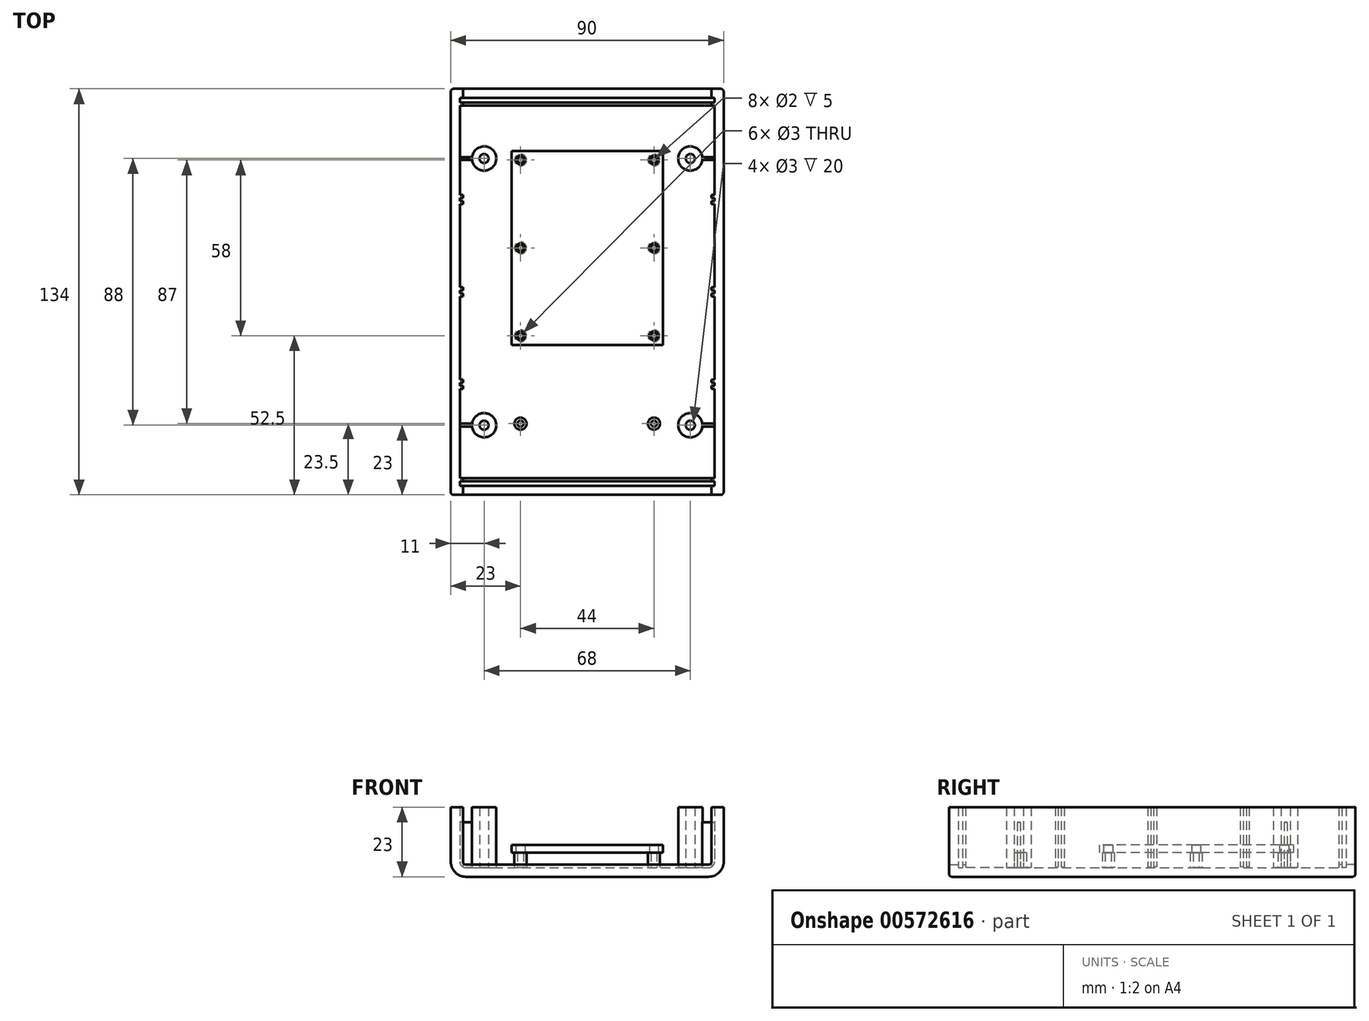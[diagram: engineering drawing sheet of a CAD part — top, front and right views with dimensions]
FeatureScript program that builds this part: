
annotation { "Feature Type Name" : "Feature", "Feature Type Description" : "" }
export const myFeature = defineFeature(function(context is Context, id is Id, definition is map)
    precondition{}
    {
        {
            var Q0;
            Q0=qCreatedBy(makeId("Top.planeOp"),FACE);
            var sketch = newSketch(context, id + "F0", { "sketchPlane" : qUnion([Q0])});
            skLineSegment(sketch, "E0.bottom", {"start": v(-44, 67) * mm, "end": v(-41, 67) * mm});
            skLineSegment(sketch, "E0.top", {"start": v(-45, 0) * mm, "end": v(-42, 0) * mm});
            skLineSegment(sketch, "E0.left", {"start": v(-45, 66) * mm, "end": v(-45, 0) * mm});
            skLineSegment(sketch, "E0.right", {"start": v(-41, 67) * mm, "end": v(-41, 64) * mm});
            skPoint(sketch, "E1.visualSharp", {"position": v(-45, 67) * mm});
            skArc(sketch, "E1.filletArc", {"start": v(-44, 67) * mm, "mid": v(-44.7, 66.7) * mm, "end": v(-45, 66) * mm});
            skLineSegment(sketch, "E2.bottom", {"start": v(-41, 64) * mm, "end": v(-42, 64) * mm});
            skLineSegment(sketch, "E2.top", {"start": v(-41, 62.5) * mm, "end": v(-42, 62.5) * mm});
            skLineSegment(sketch, "E2.right", {"start": v(-42, 64) * mm, "end": v(-42, 62.5) * mm});
            skLineSegment(sketch, "E3.trimOffspring", {"start": v(-41, 62.5) * mm, "end": v(-41, 61.5) * mm});
            skLineSegment(sketch, "E4.bottom", {"start": v(-41, 32) * mm, "end": v(-42, 32) * mm});
            skLineSegment(sketch, "E4.top", {"start": v(-41, 61.5) * mm, "end": v(-42, 61.5) * mm});
            skLineSegment(sketch, "E4.right", {"start": v(-42, 32) * mm, "end": v(-42, 61.5) * mm});
            skLineSegment(sketch, "E5.top", {"start": v(-41, 0.5) * mm, "end": v(-42, 0.5) * mm});
            skLineSegment(sketch, "E5.right", {"start": v(-42, 0) * mm, "end": v(-42, 0.5) * mm});
            skLineSegment(sketch, "E6.trimOffspring", {"start": v(-41, 32) * mm, "end": v(-41, 31) * mm});
            skPoint(sketch, "E7.orphan", {"position": v(-41, 0) * mm});
            skLineSegment(sketch, "E8.bottom", {"start": v(-41, 31) * mm, "end": v(-42, 31) * mm});
            skLineSegment(sketch, "E8.top", {"start": v(-41, 30) * mm, "end": v(-42, 30) * mm});
            skLineSegment(sketch, "E8.right", {"start": v(-42, 31) * mm, "end": v(-42, 30) * mm});
            skLineSegment(sketch, "E9.trimOffspring", {"start": v(-41, 30) * mm, "end": v(-41, 29) * mm});
            skLineSegment(sketch, "E10.bottom", {"start": v(-41, 29) * mm, "end": v(-42, 29) * mm});
            skLineSegment(sketch, "E10.top", {"start": v(-41, 1.5) * mm, "end": v(-42, 1.5) * mm});
            skLineSegment(sketch, "E10.right", {"start": v(-42, 29) * mm, "end": v(-42, 1.5) * mm});
            skLineSegment(sketch, "E11.trimOffspring", {"start": v(-41, 1.5) * mm, "end": v(-41, 0.5) * mm});
            skSolve(sketch);
        }
        {
            var Q0;
            Q0=qCreatedBy(makeId("Front.planeOp"),FACE);
            var sketch = newSketch(context, id + "F1", { "sketchPlane" : qUnion([Q0])});
            skPoint(sketch, "E12.0", {"position": v(-45, 0) * mm});
            skLineSegment(sketch, "E13", {"start": v(-45, 0) * mm, "end": v(-45, -18) * mm});
            skLineSegment(sketch, "E14", {"start": v(-40, -23) * mm, "end": v(0, -23) * mm});
            skPoint(sketch, "E15.visualSharp", {"position": v(-45, -23) * mm});
            skArc(sketch, "E15.filletArc", {"start": v(-45, -18) * mm, "mid": v(-43.54, -21.54) * mm, "end": v(-40, -23) * mm});
            skSolve(sketch);
        }
        {
            var Q0;
            Q0 = qSketchRegion(id + "F0", true);
            var Q1;
            Q1 = qConstructionFilter(qBodyType(qCreatedBy(id + "F1" ,EDGE), BodyType.WIRE), ConstructionObject.NO);
            sweep(context, id + "F2", {"profiles" : qUnion([Q0]), "path" : qUnion([Q1])});
        }
        {
            var Q0;
            Q0=qCreatedBy(makeId("Front.planeOp"),FACE);
            var sketch = newSketch(context, id + "F3", { "sketchPlane" : qUnion([Q0])});
            skLineSegment(sketch, "E16.bottom", {"start": v(0, -13.34) * mm, "end": v(-41, -13.34) * mm});
            skLineSegment(sketch, "E16.top", {"start": v(0, -20) * mm, "end": v(-40, -20) * mm});
            skLineSegment(sketch, "E16.left", {"start": v(0, -13.34) * mm, "end": v(0, -20) * mm});
            skLineSegment(sketch, "E16.right", {"start": v(-41, -13.34) * mm, "end": v(-41, -19.73) * mm});
            skLineSegment(sketch, "E17.0", {"start": v(-40, -20) * mm, "end": v(0, -20) * mm});
            skArc(sketch, "E18.0", {"start": v(-41, -19.73) * mm, "mid": v(-40.52, -19.93) * mm, "end": v(-40, -20) * mm});
            skPoint(sketch, "E19.orphan", {"position": v(-42, -18) * mm});
            skLineSegment(sketch, "E20.0", {"start": v(-41, 0) * mm, "end": v(-41, -13.34) * mm, "construction": true});
            skPoint(sketch, "E21.orphan", {"position": v(-41, -18) * mm});
            skSolve(sketch);
        }
        {
            var Q0;
            Q0 = qSketchRegion(id + "F3", true);
            extrude(context, id + "F4", {"entities" : qUnion([Q0]), "operationType" : NewBodyOperationType.REMOVE, "oppositeDirection" : true, "depth" : 40 * mm, "offsetDistance" : 25 * mm});
        }
        {
            var Q0;
            {var subQ0=sQuery(id+"F1.wireOp",EDGE,"E14");Q0=makeQuery(id+"F4.boolean.opBoolean","MERGE",FACE,{"derivedFrom":[makeQuery(id+"F2.opSweep","SWEPT_FACE",FACE,{"disambiguationData":[OSD([sQuery(id+"F0.wireOp",EDGE,"E4.right"),subQ0])]}),makeQuery(id+"F2.opSweep","SWEPT_FACE",FACE,{"disambiguationData":[OSD([sQuery(id+"F0.wireOp",EDGE,"E5.right"),subQ0])]}),makeQuery(id+"F2.opSweep","SWEPT_FACE",FACE,{"disambiguationData":[OSD([sQuery(id+"F0.wireOp",EDGE,"E8.right"),subQ0])]}),makeQuery(id+"F2.opSweep","SWEPT_FACE",FACE,{"disambiguationData":[OSD([sQuery(id+"F0.wireOp",EDGE,"E10.right"),subQ0])]}),makeQuery(id+"F4.opExtrude","SWEPT_FACE",FACE,{"disambiguationData":[OSD([sQuery(id+"F3.wireOp",EDGE,"E17.0")])]})]});}
            var sketch = newSketch(context, id + "F5", { "sketchPlane" : qUnion([Q0])});
            skCircle(sketch, "E22", {"center": v(-34, 44) * mm, "radius": 4 * mm});
            skCircle(sketch, "E23", {"center": v(-34, 44) * mm, "radius": 1.5 * mm});
            skCircle(sketch, "E24", {"center": v(-22, 43.5) * mm, "radius": 2 * mm});
            skCircle(sketch, "E25", {"center": v(-22, 43.5) * mm, "radius": 1 * mm});
            skCircle(sketch, "E26.0.1.0", {"center": v(-22, 14.5) * mm, "radius": 2 * mm});
            skCircle(sketch, "E26.0.1.1", {"center": v(-22, 14.5) * mm, "radius": 1 * mm});
            skLineSegment(sketch, "E26.direction1", {"start": v(-22, 43.5) * mm, "end": v(-7.59, 43.5) * mm, "construction": true});
            skLineSegment(sketch, "E26.direction2", {"start": v(-22, 43.5) * mm, "end": v(-22, 14.5) * mm, "construction": true});
            skLineSegment(sketch, "E27.bottom", {"start": v(-37.97, 43.5) * mm, "end": v(-42, 43.5) * mm});
            skLineSegment(sketch, "E27.top", {"start": v(-37.97, 44.5) * mm, "end": v(-42, 44.5) * mm});
            skLineSegment(sketch, "E27.right", {"start": v(-42, 43.5) * mm, "end": v(-42, 44.5) * mm});
            skPoint(sketch, "E27.middle", {"position": v(-39.98, 44) * mm});
            skSolve(sketch);
        }
        {
            var Q0;
            Q0=makeQuery(id+"F5.imprint","IMPRINT",FACE,{"disambiguationData":[TD([[makeQuery(id+"F5.imprint","IMPRINT",EDGE,{"derivedFrom":sQuery(id+"F5.wireOp",EDGE,"E22")}),1.0]])]});
            extrude(context, id + "F6", {"entities" : qUnion([Q0]), "operationType" : NewBodyOperationType.ADD, "depth" : 20 * mm, "offsetDistance" : 25 * mm});
        }
        {
            var Q0;
            {var subQ0=sQuery(id+"F5.wireOp",EDGE,"E27.right");Q0=makeQuery(id+"F5.imprint","IMPRINT",FACE,{"disambiguationData":[TD([[makeQuery(id+"F5.imprint","IMPRINT",EDGE,{"derivedFrom":subQ0}),-1.0]])]});}
            var Q1;
            {var subQ0=sQuery(id+"F5.wireOp",EDGE,"E27.bottom");var subQ1=sQuery(id+"F5.wireOp",EDGE,"E22");var subQ2=makeQuery(id+"F5.imprint","INTERSECT",VERTEX,{"derivedFrom":[subQ1,subQ0]});Q1=makeQuery(id+"F5.imprint","IMPRINT",FACE,{"disambiguationData":[TD([[makeQuery(id+"F5.imprint","IMPRINT",EDGE,{"disambiguationData":[TD([[subQ2,1.0]])],"derivedFrom":subQ1}),-1.0]])]});}
            extrude(context, id + "F7", {"entities" : qUnion([Q0, Q1]), "operationType" : NewBodyOperationType.ADD, "depth" : 15 * mm, "offsetDistance" : 25 * mm});
        }
        {
            var Q0;
            Q0=makeQuery(id+"F5.imprint","IMPRINT",FACE,{"disambiguationData":[TD([[makeQuery(id+"F5.imprint","IMPRINT",EDGE,{"derivedFrom":sQuery(id+"F5.wireOp",EDGE,"E24")}),1.0]])]});
            var Q1;
            Q1=makeQuery(id+"F5.imprint","IMPRINT",FACE,{"disambiguationData":[TD([[makeQuery(id+"F5.imprint","IMPRINT",EDGE,{"derivedFrom":sQuery(id+"F5.wireOp",EDGE,"E26.0.1.0")}),1.0]])]});
            extrude(context, id + "F8", {"entities" : qUnion([Q0, Q1]), "operationType" : NewBodyOperationType.ADD, "depth" : 5 * mm, "offsetDistance" : 25 * mm});
        }
        {
            var Q0;
            Q0=makeQuery(id+"F2.opSweep","SWEPT_BODY",BODY,{"disambiguationData":[OSD([sQuery(id+"F0.wireOp",EDGE,"E0.bottom"),sQuery(id+"F0.wireOp",EDGE,"E0.top"),sQuery(id+"F0.wireOp",EDGE,"E0.left"),sQuery(id+"F0.wireOp",EDGE,"E0.right"),sQuery(id+"F0.wireOp",EDGE,"E1.filletArc"),sQuery(id+"F0.wireOp",EDGE,"E2.bottom"),sQuery(id+"F0.wireOp",EDGE,"E2.top"),sQuery(id+"F0.wireOp",EDGE,"E2.right"),sQuery(id+"F0.wireOp",EDGE,"E3.trimOffspring"),sQuery(id+"F0.wireOp",EDGE,"E4.bottom"),sQuery(id+"F0.wireOp",EDGE,"E4.top"),sQuery(id+"F0.wireOp",EDGE,"E4.right"),sQuery(id+"F0.wireOp",EDGE,"E5.top"),sQuery(id+"F0.wireOp",EDGE,"E5.right"),sQuery(id+"F0.wireOp",EDGE,"E6.trimOffspring"),sQuery(id+"F0.wireOp",EDGE,"E8.bottom"),sQuery(id+"F0.wireOp",EDGE,"E8.top"),sQuery(id+"F0.wireOp",EDGE,"E8.right"),sQuery(id+"F0.wireOp",EDGE,"E9.trimOffspring"),sQuery(id+"F0.wireOp",EDGE,"E10.bottom"),sQuery(id+"F0.wireOp",EDGE,"E10.top"),sQuery(id+"F0.wireOp",EDGE,"E10.right"),sQuery(id+"F0.wireOp",EDGE,"E11.trimOffspring"),sQuery(id+"F1.wireOp",EDGE,"E14")])]});
            var Q1;
            Q1=makeQuery(id+"F2.opSweep","SWEPT_FACE",FACE,{"disambiguationData":[OSD([sQuery(id+"F0.wireOp",EDGE,"E0.top"),sQuery(id+"F1.wireOp",EDGE,"E13")])]});
            mirror(context, id + "F9", {"operationType" : NewBodyOperationType.ADD, "entities" : qUnion([Q0]), "mirrorPlane" : qUnion([Q1])});
        }
        {
            var Q0;
            Q0=makeQuery(id+"F2.opSweep","SWEPT_BODY",BODY,{"disambiguationData":[OSD([sQuery(id+"F0.wireOp",EDGE,"E0.bottom"),sQuery(id+"F0.wireOp",EDGE,"E0.top"),sQuery(id+"F0.wireOp",EDGE,"E0.left"),sQuery(id+"F0.wireOp",EDGE,"E0.right"),sQuery(id+"F0.wireOp",EDGE,"E1.filletArc"),sQuery(id+"F0.wireOp",EDGE,"E2.bottom"),sQuery(id+"F0.wireOp",EDGE,"E2.top"),sQuery(id+"F0.wireOp",EDGE,"E2.right"),sQuery(id+"F0.wireOp",EDGE,"E3.trimOffspring"),sQuery(id+"F0.wireOp",EDGE,"E4.bottom"),sQuery(id+"F0.wireOp",EDGE,"E4.top"),sQuery(id+"F0.wireOp",EDGE,"E4.right"),sQuery(id+"F0.wireOp",EDGE,"E5.top"),sQuery(id+"F0.wireOp",EDGE,"E5.right"),sQuery(id+"F0.wireOp",EDGE,"E6.trimOffspring"),sQuery(id+"F0.wireOp",EDGE,"E8.bottom"),sQuery(id+"F0.wireOp",EDGE,"E8.top"),sQuery(id+"F0.wireOp",EDGE,"E8.right"),sQuery(id+"F0.wireOp",EDGE,"E9.trimOffspring"),sQuery(id+"F0.wireOp",EDGE,"E10.bottom"),sQuery(id+"F0.wireOp",EDGE,"E10.top"),sQuery(id+"F0.wireOp",EDGE,"E10.right"),sQuery(id+"F0.wireOp",EDGE,"E11.trimOffspring"),sQuery(id+"F1.wireOp",EDGE,"E14")])]});
            var Q1;
            {var subQ0=makeQuery(id+"F2.opSweep","CAP_FACE",FACE,{"disambiguationData":[OSD([sQuery(id+"F0.wireOp",EDGE,"E0.bottom"),sQuery(id+"F0.wireOp",EDGE,"E0.top"),sQuery(id+"F0.wireOp",EDGE,"E0.left"),sQuery(id+"F0.wireOp",EDGE,"E0.right"),sQuery(id+"F0.wireOp",EDGE,"E1.filletArc"),sQuery(id+"F0.wireOp",EDGE,"E2.bottom"),sQuery(id+"F0.wireOp",EDGE,"E2.top"),sQuery(id+"F0.wireOp",EDGE,"E2.right"),sQuery(id+"F0.wireOp",EDGE,"E3.trimOffspring"),sQuery(id+"F0.wireOp",EDGE,"E4.bottom"),sQuery(id+"F0.wireOp",EDGE,"E4.top"),sQuery(id+"F0.wireOp",EDGE,"E4.right"),sQuery(id+"F0.wireOp",EDGE,"E5.top"),sQuery(id+"F0.wireOp",EDGE,"E5.right"),sQuery(id+"F0.wireOp",EDGE,"E6.trimOffspring"),sQuery(id+"F0.wireOp",EDGE,"E8.bottom"),sQuery(id+"F0.wireOp",EDGE,"E8.top"),sQuery(id+"F0.wireOp",EDGE,"E8.right"),sQuery(id+"F0.wireOp",EDGE,"E9.trimOffspring"),sQuery(id+"F0.wireOp",EDGE,"E10.bottom"),sQuery(id+"F0.wireOp",EDGE,"E10.top"),sQuery(id+"F0.wireOp",EDGE,"E10.right"),sQuery(id+"F0.wireOp",EDGE,"E11.trimOffspring"),sQuery(id+"F1.wireOp",VERTEX,"E14.end")])],"isStart":false});Q1=makeQuery(id+"F9.boolean.opBoolean","MERGE",FACE,{"derivedFrom":[subQ0,makeQuery(id+"F9.opPattern","COPY",FACE,{"derivedFrom":subQ0,"instanceName":"1"})]});}
            mirror(context, id + "F10", {"operationType" : NewBodyOperationType.ADD, "entities" : qUnion([Q0]), "mirrorPlane" : qUnion([Q1])});
        }
        {
            var Q0;
            Q0=makeQuery(id+"F8.opExtrude","CAP_FACE",FACE,{"disambiguationData":[OSD([sQuery(id+"F5.wireOp",EDGE,"E24"),sQuery(id+"F5.wireOp",EDGE,"E25")])],"isStart":false});
            var sketch = newSketch(context, id + "F11", { "sketchPlane" : qUnion([Q0])});
            skCircle(sketch, "E28", {"center": v(-22, 43.5) * mm, "radius": 3 * mm, "construction": true});
            skCircle(sketch, "E29", {"center": v(22, -14.5) * mm, "radius": 3 * mm, "construction": true});
            skLineSegment(sketch, "E30.bottom", {"start": v(-25, 46.5) * mm, "end": v(25, 46.5) * mm});
            skLineSegment(sketch, "E30.top", {"start": v(-25, -17.5) * mm, "end": v(25, -17.5) * mm});
            skLineSegment(sketch, "E30.left", {"start": v(-25, 46.5) * mm, "end": v(-25, -17.5) * mm});
            skLineSegment(sketch, "E30.right", {"start": v(25, 46.5) * mm, "end": v(25, -17.5) * mm});
            skCircle(sketch, "E31", {"center": v(-22, 43.5) * mm, "radius": 1.5 * mm});
            skCircle(sketch, "E32", {"center": v(22, 43.5) * mm, "radius": 1.5 * mm});
            skCircle(sketch, "E33", {"center": v(22, 14.5) * mm, "radius": 1.5 * mm});
            skCircle(sketch, "E34", {"center": v(22, -14.5) * mm, "radius": 1.5 * mm});
            skCircle(sketch, "E35", {"center": v(-22, 14.5) * mm, "radius": 1.5 * mm});
            skCircle(sketch, "E36", {"center": v(-22, -14.5) * mm, "radius": 1.5 * mm});
            skSolve(sketch);
        }
        {
            var Q0;
            Q0 = qSketchRegion(id + "F11", true);
            extrude(context, id + "F12", {"entities" : qUnion([Q0]), "depth" : 2.5 * mm, "offsetDistance" : 25 * mm});
        }
    });
